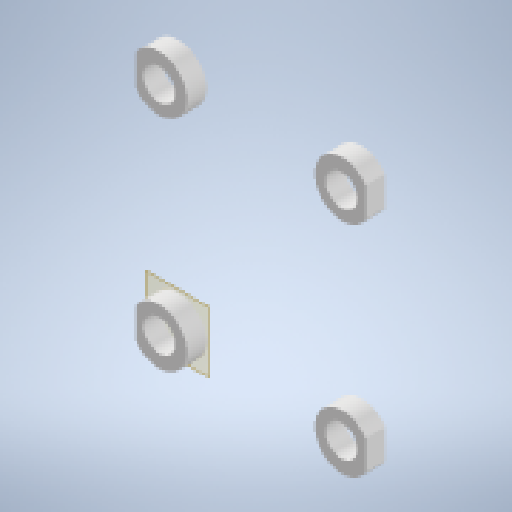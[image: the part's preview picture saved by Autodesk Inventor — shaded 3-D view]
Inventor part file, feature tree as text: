
AUTODESK INVENTOR PART (.ipt)
format: ipt  version: 2024.2 (Build 282272000, 272)  size: 329,216 bytes
history: native  units: mm
features: other x18, projected_geometry x15, sketch x5, extrude x4, reference x4
ambient origin geometry x8: Origin, YZ Plane, XZ Plane, XY Plane, X Axis, Y Axis, Z Axis, Center Point
bodies: Body1 (feature_tree)
feature tree (46):
  other  "Твердое тело1"
  other  "РабПлоскость1"
  extrude  "Выдавливание1"  Depth=2.0mm TaperAngle=0.0deg
  extrude  "Выдавливание2"  Depth=24.0mm TaperAngle=0.0deg
  other  "Сопряжение грани1"
  other  "Сопряжение грани2"
  other  "Сопряжение грани3"
  other  "Сопряжение грани4"
  other  "Сопряжение грани5"
  other  "Сопряжение грани6"
  other  "Сопряжение грани7"
  other  "Сопряжение грани8"
  extrude  "Выдавливание3"  Depth=1.0mm
  other  "Сопряжение грани9"
  other  "Сопряжение грани10"
  other  "Сопряжение грани11"
  other  "Сопряжение грани12"
  extrude  "Выдавливание4"  Depth=1.0mm
  other  "РабПлоскость2"
  other  "РабПлоскость3"
  sketch  "Эскиз2"
  sketch  "Эскиз1"
  reference  "Ссылка1"
  reference  "Ссылка2"
  reference  "Ссылка3"
  reference  "Ссылка4"
  sketch  "Эскиз3"
  projected_geometry  "Спроецированная петля1"
  projected_geometry  "Спроецированная петля2"
  projected_geometry  "Спроецированная петля3"
  projected_geometry  "Спроецированная петля4"
  projected_geometry  "Спроецированная петля5"
  projected_geometry  "Спроецированная петля6"
  projected_geometry  "Спроецированная петля7"
  projected_geometry  "Спроецированная петля8"
  projected_geometry  "Спроецированная петля9"
  projected_geometry  "Спроецированная петля10"
  projected_geometry  "Спроецированная петля11"
  projected_geometry  "Спроецированная петля12"
  projected_geometry  "Спроецированная петля13"
  projected_geometry  "Спроецированная петля14"
  sketch  "Эскиз4"
  sketch  "Эскиз5"
  projected_geometry  "Спроецированная петля15"
  other  "<userpath>\Documents\Artist\3D\каретка.iam"
  other  "каретка.iam"
